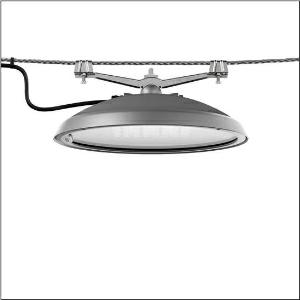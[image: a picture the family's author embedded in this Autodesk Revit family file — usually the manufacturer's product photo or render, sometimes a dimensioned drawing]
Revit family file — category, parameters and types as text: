
# Revit family: dl_50_iq_mini___p1_0s_5xa248u41f08fe_51d4
name_source: partatom
category: Lighting Fixtures
units: mm (PartAtom-declared; Revit-internal decimal feet)

## family parameters
Cut with Voids When Loaded = No
Host = Face
Light Source = No
Part Type = Normal
Room Calculation Point = No
Round Connector Dimension = Use Diameter
Shared = No

## types (1)
- --- (1 x LED, 2610 lm, 15.7 W, 4000K)
    Apparent Load = 16 VA
    CIE Flux Codes = 23 54 93 100 100
    Color Rendering = 70
    Color Temperature = 4000K
    Default Elevation = 1800 mm
    Description = DL 50 iQ mini, catenary luminaire, primary light control with lens, of PMMA, primary optical cover: cover, of toughened safety glass, transparent, light distribution: P1.0s, light emission: direct distribution, primary light characteristic: symmetric, installation type: suspended mounting, LED, High Power LED, rated luminous flux: 2.610lm, luminous efficacy: 166lm/W, light colour: 740, colour temperature: 4000K, control gear: iQ Street-Remote, control: optimised constant luminous flux control (CLO 2.0), Desk-Remote (wireless, voltage-free reading and setting of iQ features in the workshop via application-optimized NFC function/RFID function), Light-Fading, Smart-Wire, Night-Set, Lumen-Switch, Temp-Guard, Auto-Match, Street-Remote, mains connection: 230..240V, AC, 50/60Hz, start of lifetime: 16W, end of service life: 16W, reduction: 8W, luminaire housing, of diecast aluminium, powder-coated, SITECO metallic grey (DB 702S), diameter: 500mm, height: 115mm, mounting height: 4..12m, protection rating (complete): IP66, insulation class (complete): insulation class II (safety insulation), certification: CE, ENEC, ENEC+, VDE, impact resistance: IK08, permissible operating ambient temperature for outdoor applications: -25..+40°C, standard-compliant lighting for roads and squares, packaging unit: 1 piece

Light Distribution: P1.0s
    Height = 124 mm  [stored 0.406824 ft]
    Lamp = 1 x LED
    Lamp Light Flux = 2610 lm
    Lamp Power = 15.7 W
    Lamp count = 1
    Length = 500 mm
    Luminous efficacy = 166 lm/W
    Manufacturer = Siteco
    ModVariant = No
    Model = 5XA248U41F08FE
    Number of Poles = 1
    OnlyDefault = Yes
    Power Factor = 1
    Product Name = DL 50 iQ mini | P1.0s
    Product group = catenary luminaire
    ProductGroupID = 6300
    Protection Class = Protection class II
    Protection Degree = IP 66
    RLX_Detail_Level = 1
    RLX_Emergency_Light_Flux = 0 lm
    RLX_Emergency_Type = 0
    RLX_Emergency_Type_DB = No
    RlxData = <blob elided: 123137 chars, md5=a13dab43>
    Socket = socket
    Standby Power = 0 W
    System Light Flux = 2610 lm
    System Power = 16 W
    Type Comments = factory setting: luminous flux: 100 % | dim-lin: 254 | 319 mA
    Type Image = l_1242791.jpg
    URL = http://relux.com
    VarID = @adj_138811
    Voltage = 0 V
    Weight = 0.00 kg
    Width = 0 mm  [stored 0 ft]

note: [stored X ft] marks values corroborated as IEEE doubles in the binary element streams (Revit-internal decimal feet)

## geometry (parser evidence)
native form markers: Blend x4, Sweep x15
no freeform markers — native parametric forms only
